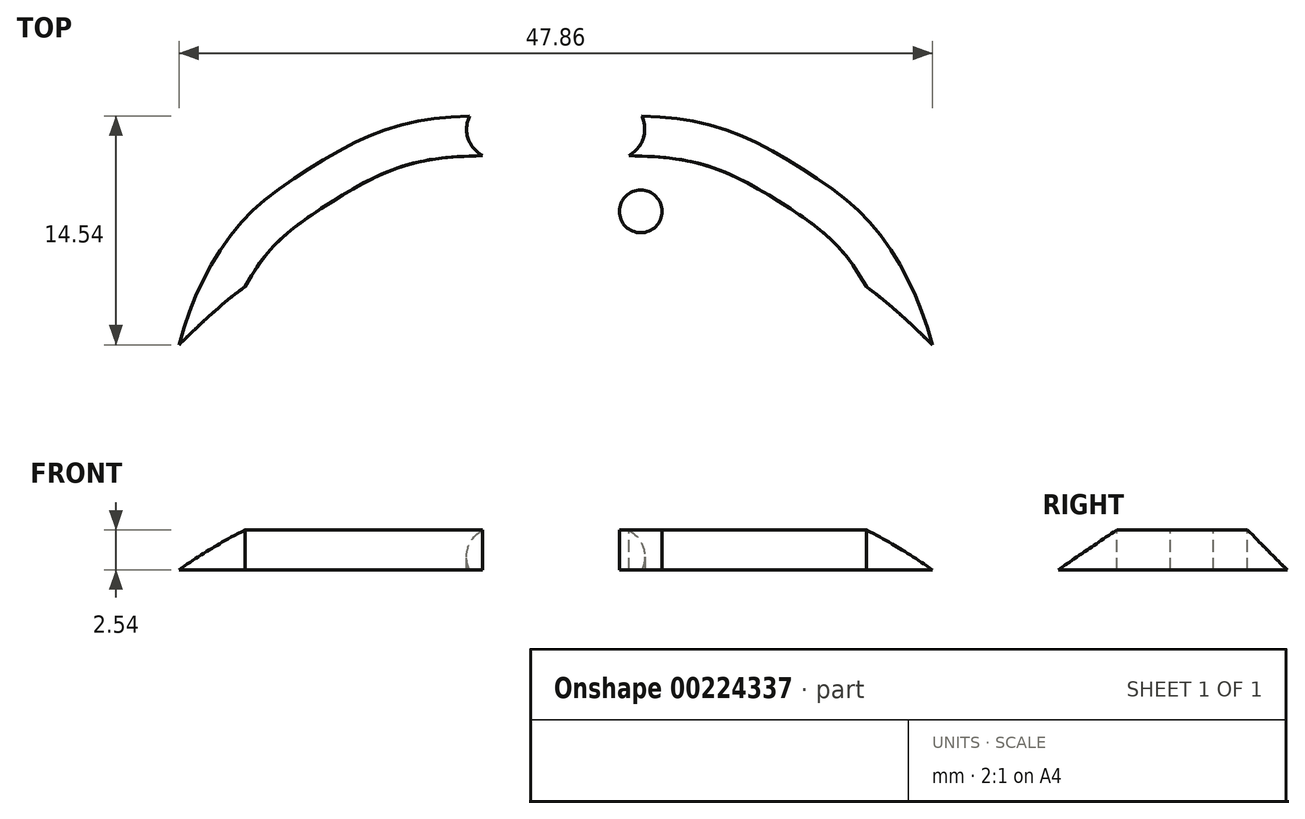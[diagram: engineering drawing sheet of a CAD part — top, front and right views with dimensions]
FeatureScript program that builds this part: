
annotation { "Feature Type Name" : "Feature", "Feature Type Description" : "" }
export const myFeature = defineFeature(function(context is Context, id is Id, definition is map)
    precondition{}
    {
        {
            var Q0;
            Q0=qCreatedBy(makeId("Top.planeOp"),FACE);
            var sketch = newSketch(context, id + "F0", { "sketchPlane" : qUnion([Q0])});
            skFitSpline(sketch, "E0", {"points": [v(0, 0) * mm, v(-1.5, 4) * mm, v(-5, 8.42) * mm, v(-10.93, 10.84) * mm, v(-16.52, 10.1) * mm, v(-21.35, 6.92) * mm, v(-25.69, 2.75) * mm], "startDerivative": vector(-8.47, 27.18) * mm, "endDerivative": vector(-24.48, -24.86) * mm});
            skFitSpline(sketch, "E1", {"points": [v(-25.69, 2.75) * mm, v(-24.28, 7.5) * mm, v(-21.19, 12.84) * mm, v(-17.02, 16.35) * mm, v(-11.35, 19.35) * mm, v(-6.68, 20.26) * mm, v(-3.76, 20.35) * mm], "startDerivative": vector(6.82, 28.12) * mm, "endDerivative": vector(21.78, 0.05) * mm});
            skFitSpline(sketch, "E2", {"points": [v(-3.76, 20.35) * mm, v(-5.38, 19.18) * mm, v(-5.6, 17.72) * mm, v(-4.68, 16.56) * mm, v(-2.24, 15.52) * mm], "startDerivative": vector(-7.46, -3.84) * mm, "endDerivative": vector(8.81, -3.18) * mm});
            skLineSegment(sketch, "E3", {"start": v(-2.24, 15.52) * mm, "end": v(-2.24, 18.7) * mm});
            skLineSegment(sketch, "E4", {"start": v(-2.24, 18.7) * mm, "end": v(-0.87, 17.16) * mm});
            skLineSegment(sketch, "E5", {"start": v(-0.87, 17.16) * mm, "end": v(0, 17.16) * mm});
            skFitSpline(sketch, "E6.MirrorCS", {"points": [v(0, 0) * mm, v(1.5, 4) * mm, v(5, 8.42) * mm, v(10.93, 10.84) * mm, v(16.52, 10.1) * mm, v(21.35, 6.92) * mm, v(25.69, 2.75) * mm], "startDerivative": vector(8.47, 27.18) * mm, "endDerivative": vector(24.48, -24.86) * mm});
            skFitSpline(sketch, "E7.MirrorCS", {"points": [v(25.69, 2.75) * mm, v(24.28, 7.5) * mm, v(21.19, 12.84) * mm, v(17.02, 16.35) * mm, v(11.35, 19.35) * mm, v(6.68, 20.26) * mm, v(3.76, 20.35) * mm], "startDerivative": vector(-6.82, 28.12) * mm, "endDerivative": vector(-21.78, 0.05) * mm});
            skFitSpline(sketch, "E8.MirrorCS", {"points": [v(3.76, 20.35) * mm, v(5.38, 19.18) * mm, v(5.6, 17.72) * mm, v(4.68, 16.56) * mm, v(2.24, 15.52) * mm], "startDerivative": vector(7.46, -3.84) * mm, "endDerivative": vector(-8.81, -3.18) * mm});
            skLineSegment(sketch, "E9.MirrorCS", {"start": v(2.24, 15.52) * mm, "end": v(2.24, 18.7) * mm});
            skLineSegment(sketch, "E10.MirrorCS", {"start": v(2.24, 18.7) * mm, "end": v(0.87, 17.16) * mm});
            skLineSegment(sketch, "E11.MirrorCS", {"start": v(0.87, 17.16) * mm, "end": v(0, 17.16) * mm});
            skSolve(sketch);
        }
        {
            var Q0;
            Q0=makeQuery(id+"F0.imprint","IMPRINT",FACE,{"disambiguationData":[TD([[makeQuery(id+"F0.imprint","IMPRINT",EDGE,{"derivedFrom":sQuery(id+"F0.wireOp",EDGE,"E0")}),-1.0]])]});
            extrude(context, id + "F1", {"entities" : qUnion([Q0]), "depth" : 2.54 * mm});
        }
        {
            var Q0;
            Q0=makeQuery(id+"F1.opExtrude","CAP_EDGE",EDGE,{"disambiguationData":[OSD([sQuery(id+"F0.wireOp",EDGE,"E1")])],"isStart":false});
            var Q1;
            Q1=makeQuery(id+"F1.opExtrude","CAP_EDGE",EDGE,{"disambiguationData":[OSD([sQuery(id+"F0.wireOp",EDGE,"E7.MirrorCS")])],"isStart":false});
            chamfer(context, id + "F2", {"entities" : qUnion([Q0, Q1]), "width" : 3.8 * mm, "tangentPropagation" : true});
        }
        {
            var Q0;
            Q0=makeQuery(id+"F1.opExtrude","CAP_FACE",FACE,{"disambiguationData":[OSD([sQuery(id+"F0.wireOp",EDGE,"E0"),sQuery(id+"F0.wireOp",EDGE,"E1"),sQuery(id+"F0.wireOp",EDGE,"E2"),sQuery(id+"F0.wireOp",EDGE,"E3"),sQuery(id+"F0.wireOp",EDGE,"E4"),sQuery(id+"F0.wireOp",EDGE,"E5"),sQuery(id+"F0.wireOp",EDGE,"E6.MirrorCS"),sQuery(id+"F0.wireOp",EDGE,"E7.MirrorCS"),sQuery(id+"F0.wireOp",EDGE,"E8.MirrorCS"),sQuery(id+"F0.wireOp",EDGE,"E9.MirrorCS"),sQuery(id+"F0.wireOp",EDGE,"E10.MirrorCS"),sQuery(id+"F0.wireOp",EDGE,"E11.MirrorCS")])],"isStart":false});
            var sketch = newSketch(context, id + "F3", { "sketchPlane" : qUnion([Q0])});
            skArc(sketch, "E12", {"start": v(0, 11.52) * mm, "mid": v(-1.36, 10.16) * mm, "end": v(0, 8.8) * mm});
            skCircle(sketch, "E13", {"center": v(-5.4, 13) * mm, "radius": 1.36 * mm});
            skArc(sketch, "E14.MirrorCS", {"start": v(0, 11.52) * mm, "mid": v(1.36, 10.16) * mm, "end": v(0, 8.8) * mm});
            skCircle(sketch, "E15.MirrorC", {"center": v(5.4, 13) * mm, "radius": 1.36 * mm});
            skSolve(sketch);
        }
        {
            var Q0;
            Q0=makeQuery(id+"F3.imprint","IMPRINT",FACE,{"disambiguationData":[TD([[makeQuery(id+"F3.imprint","IMPRINT",EDGE,{"derivedFrom":sQuery(id+"F3.wireOp",EDGE,"E12")}),1.0]])]});
            var Q1;
            Q1=makeQuery(id+"F3.imprint","IMPRINT",FACE,{"disambiguationData":[TD([[makeQuery(id+"F3.imprint","IMPRINT",EDGE,{"derivedFrom":sQuery(id+"F3.wireOp",EDGE,"E15.MirrorC")}),-1.0]])]});
            var Q2;
            Q2=makeQuery(id+"F3.imprint","IMPRINT",FACE,{"disambiguationData":[TD([[makeQuery(id+"F3.imprint","IMPRINT",EDGE,{"derivedFrom":sQuery(id+"F3.wireOp",EDGE,"E13")}),1.0]])]});
            extrude(context, id + "F4", {"entities" : qUnion([Q0, Q1, Q2]), "operationType" : NewBodyOperationType.REMOVE, "oppositeDirection" : true, "depth" : 25.4 * mm});
        }
    });
